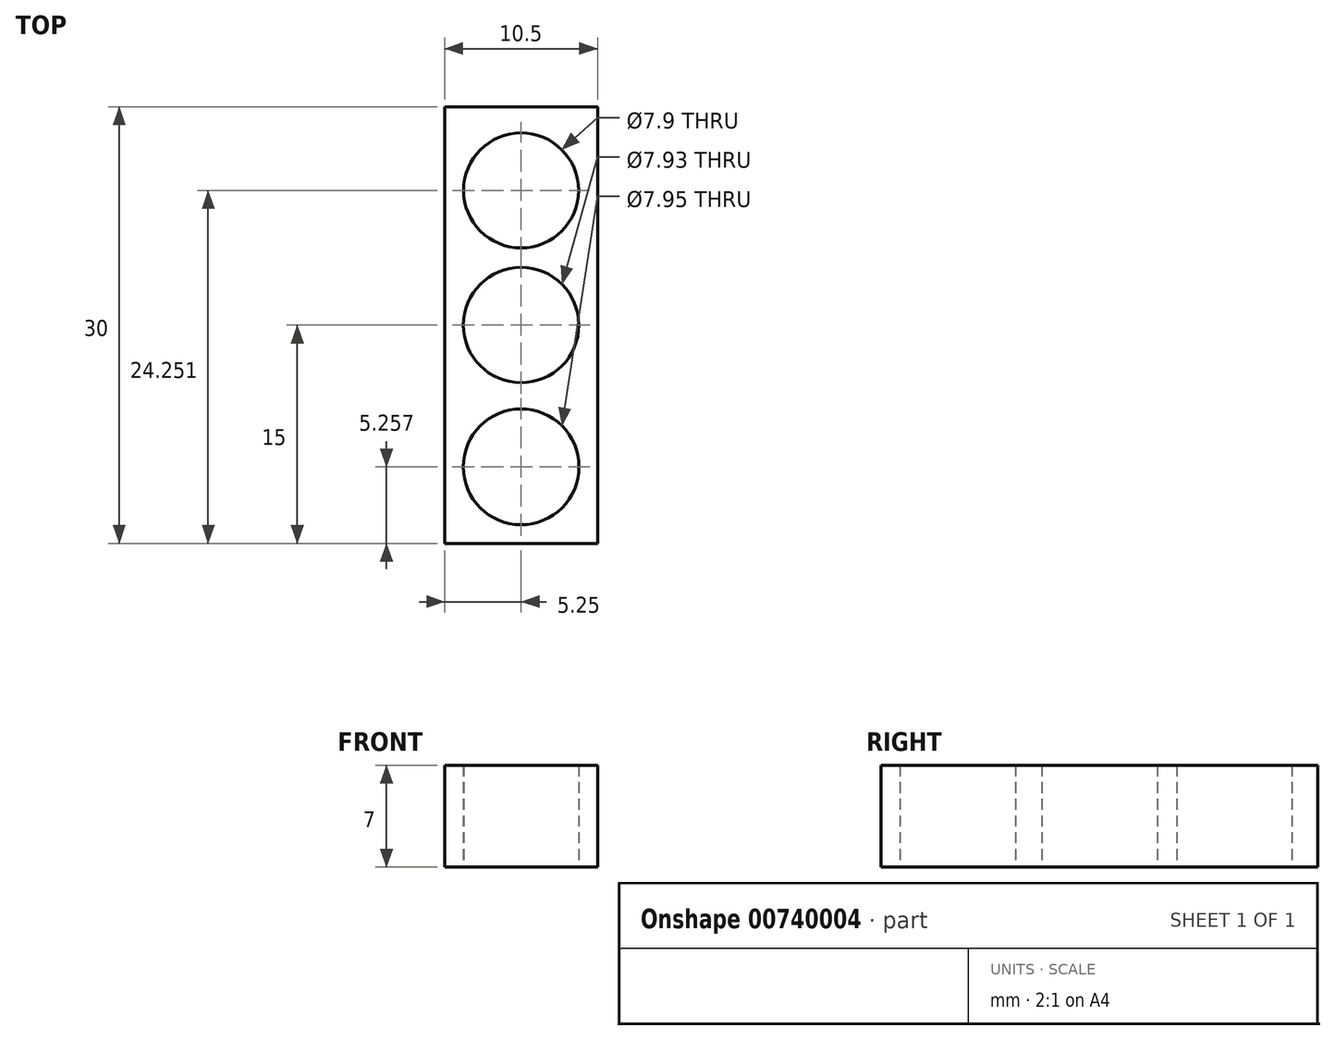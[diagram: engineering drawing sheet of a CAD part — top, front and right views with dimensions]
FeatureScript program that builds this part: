
annotation { "Feature Type Name" : "Feature", "Feature Type Description" : "" }
export const myFeature = defineFeature(function(context is Context, id is Id, definition is map)
    precondition{}
    {
        {
            var Q0;
            Q0=qCreatedBy(makeId("Top.planeOp"),FACE);
            var sketch = newSketch(context, id + "F0", { "sketchPlane" : qUnion([Q0])});
            skLineSegment(sketch, "E0.bottom", {"start": v(5.25, -15) * mm, "end": v(-5.25, -15) * mm});
            skLineSegment(sketch, "E0.top", {"start": v(5.25, 15) * mm, "end": v(-5.25, 15) * mm});
            skLineSegment(sketch, "E0.left", {"start": v(5.25, -15) * mm, "end": v(5.25, 15) * mm});
            skLineSegment(sketch, "E0.right", {"start": v(-5.25, -15) * mm, "end": v(-5.25, 15) * mm});
            skPoint(sketch, "E0.middle", {"position": v(0, 0) * mm});
            skCircle(sketch, "E1", {"center": v(0, 9.25) * mm, "radius": 3.95 * mm});
            skPoint(sketch, "E1.centerSnap0", {"position": v(0, 15) * mm});
            skCircle(sketch, "E2", {"center": v(0, 0) * mm, "radius": 3.96 * mm});
            skCircle(sketch, "E3", {"center": v(0, -9.74) * mm, "radius": 3.98 * mm});
            skSolve(sketch);
        }
        {
            var Q0;
            Q0=makeQuery(id+"F0.imprint","IMPRINT",FACE,{"disambiguationData":[TD([[makeQuery(id+"F0.imprint","IMPRINT",EDGE,{"derivedFrom":sQuery(id+"F0.wireOp",EDGE,"E0.bottom")}),-1.0]])]});
            extrude(context, id + "F1", {"entities" : qUnion([Q0]), "depth" : 7 * mm, "offsetDistance" : 25 * mm});
        }
    });
